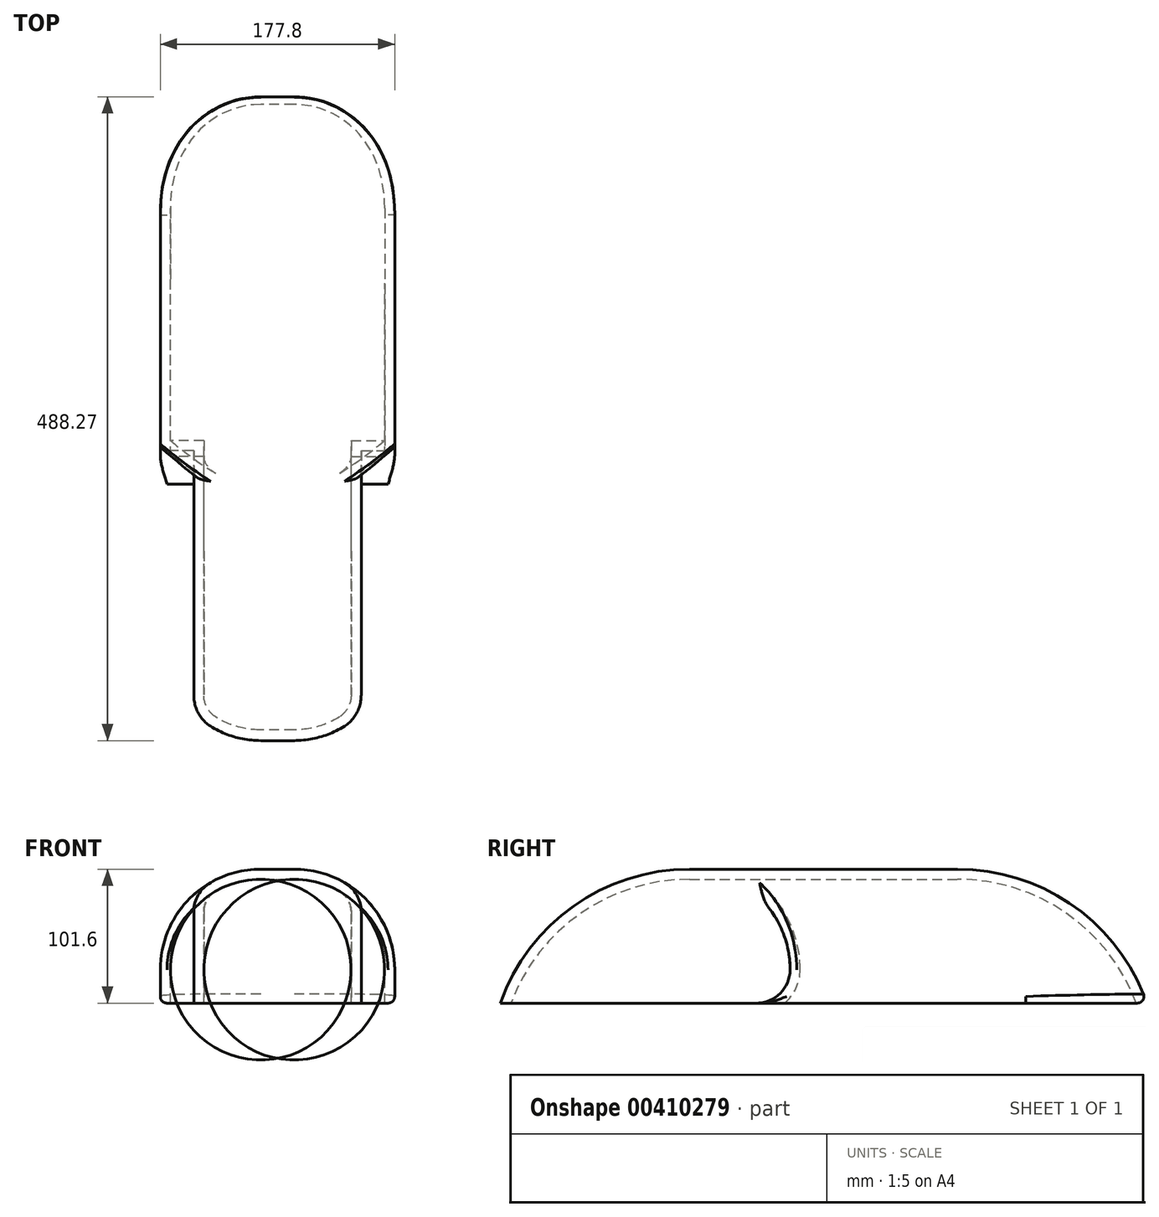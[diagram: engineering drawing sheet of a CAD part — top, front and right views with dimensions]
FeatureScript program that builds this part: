
annotation { "Feature Type Name" : "Feature", "Feature Type Description" : "" }
export const myFeature = defineFeature(function(context is Context, id is Id, definition is map)
    precondition{}
    {
        {
            var Q0;
            Q0=qCreatedBy(makeId("Right.planeOp"),FACE);
            var sketch = newSketch(context, id + "F0", { "sketchPlane" : qUnion([Q0])});
            skLineSegment(sketch, "E0.bottom", {"start": v(8.72, 0) * mm, "end": v(499.28, 0) * mm});
            skLineSegment(sketch, "E0.top", {"start": v(152.4, 101.6) * mm, "end": v(355.6, 101.6) * mm});
            skPoint(sketch, "E1.visualSharp", {"position": v(0, 101.6) * mm});
            skArc(sketch, "E1.filletArc", {"start": v(152.4, 101.6) * mm, "mid": v(64.41, 73.63) * mm, "end": v(8.72, 0) * mm});
            skPoint(sketch, "E2.visualSharp", {"position": v(508, 101.6) * mm});
            skArc(sketch, "E2.filletArc", {"start": v(499.28, 0) * mm, "mid": v(443.59, 73.63) * mm, "end": v(355.6, 101.6) * mm});
            skPoint(sketch, "E3.orphan", {"position": v(0, 0) * mm});
            skSolve(sketch);
        }
        {
            var Q0;
            Q0=makeQuery(id+"F0.imprint","IMPRINT",FACE,{"disambiguationData":[TD([[makeQuery(id+"F0.imprint","IMPRINT",EDGE,{"derivedFrom":sQuery(id+"F0.wireOp",EDGE,"E0.bottom")}),1.0]])]});
            extrude(context, id + "F1", {"entities" : qUnion([Q0]), "depth" : 177.8 * mm});
        }
        {
            var Q0;
            Q0=makeQuery(id+"F1.opExtrude","CAP_EDGE",EDGE,{"disambiguationData":[OSD([sQuery(id+"F0.wireOp",EDGE,"E1.filletArc")])],"isStart":false});
            var Q1;
            Q1=makeQuery(id+"F1.opExtrude","CAP_EDGE",EDGE,{"disambiguationData":[OSD([sQuery(id+"F0.wireOp",EDGE,"E0.top")])],"isStart":false});
            var Q2;
            Q2=makeQuery(id+"F1.opExtrude","CAP_EDGE",EDGE,{"disambiguationData":[OSD([sQuery(id+"F0.wireOp",EDGE,"E2.filletArc")])],"isStart":false});
            var Q3;
            Q3=makeQuery(id+"F1.opExtrude","CAP_EDGE",EDGE,{"disambiguationData":[OSD([sQuery(id+"F0.wireOp",EDGE,"E2.filletArc")])],"isStart":true});
            var Q4;
            Q4=makeQuery(id+"F1.opExtrude","CAP_EDGE",EDGE,{"disambiguationData":[OSD([sQuery(id+"F0.wireOp",EDGE,"E0.top")])],"isStart":true});
            var Q5;
            Q5=makeQuery(id+"F1.opExtrude","CAP_EDGE",EDGE,{"disambiguationData":[OSD([sQuery(id+"F0.wireOp",EDGE,"E1.filletArc")])],"isStart":true});
            fillet(context, id + "F2", {"entities" : qUnion([Q0, Q1, Q2, Q3, Q4, Q5]), "radius" : 76.2 * mm, "tangentPropagation" : true, "allowEdgeOverflow" : false});
        }
        {
            var Q0;
            Q0=qCreatedBy(makeId("Right.planeOp"),FACE);
            cPlane(context, id + "F3", {"entities" : qUnion([Q0]), "cplaneType" : CPlaneType.OFFSET, "offset" : 101.6 * mm, "width" : 152.4 * mm, "height" : 152.4 * mm});
        }
        {
            var Q0;
            Q0=qCreatedBy(id+"F3.planeOp",FACE);
            cPlane(context, id + "F4", {"entities" : qUnion([Q0]), "cplaneType" : CPlaneType.OFFSET, "offset" : 101.6 * mm, "width" : 152.4 * mm, "height" : 152.4 * mm});
        }
        {
            var Q0;
            Q0=qCreatedBy(id+"F4.planeOp",FACE);
            var sketch = newSketch(context, id + "F5", { "sketchPlane" : qUnion([Q0])});
            skLineSegment(sketch, "E4.bottom", {"start": v(8.71, 0) * mm, "end": v(203.2, 0) * mm});
            skLineSegment(sketch, "E4.top", {"start": v(152.4, 101.6) * mm, "end": v(152.4, 101.6) * mm});
            skLineSegment(sketch, "E4.right", {"start": v(228.6, 25.4) * mm, "end": v(228.6, 25.4) * mm});
            skPoint(sketch, "E5.visualSharp", {"position": v(0, 101.6) * mm});
            skArc(sketch, "E5.filletArc", {"start": v(152.4, 101.6) * mm, "mid": v(64.4, 73.63) * mm, "end": v(8.71, 0) * mm});
            skPoint(sketch, "E6.visualSharp", {"position": v(228.6, 101.6) * mm});
            skArc(sketch, "E6.filletArc", {"start": v(228.6, 25.4) * mm, "mid": v(206.28, 79.28) * mm, "end": v(152.4, 101.6) * mm});
            skPoint(sketch, "E7.visualSharp", {"position": v(228.6, 0) * mm});
            skArc(sketch, "E7.filletArc", {"start": v(203.2, 0) * mm, "mid": v(221.16, 7.44) * mm, "end": v(228.6, 25.4) * mm});
            skPoint(sketch, "E8.orphan", {"position": v(0, 0) * mm});
            skSolve(sketch);
        }
        {
            var Q0;
            Q0 = qSketchRegion(id + "F5", true);
            extrude(context, id + "F6", {"entities" : qUnion([Q0]), "operationType" : NewBodyOperationType.REMOVE, "oppositeDirection" : true, "depth" : 50.8 * mm});
        }
        {
            var Q0;
            Q0=qCreatedBy(makeId("Right.planeOp"),FACE);
            var sketch = newSketch(context, id + "F7", { "sketchPlane" : qUnion([Q0])});
            skLineSegment(sketch, "E9.bottom", {"start": v(8.71, 0) * mm, "end": v(203.2, 0) * mm});
            skLineSegment(sketch, "E9.top", {"start": v(152.4, 101.6) * mm, "end": v(152.4, 101.6) * mm});
            skLineSegment(sketch, "E9.right", {"start": v(228.6, 25.4) * mm, "end": v(228.6, 25.4) * mm});
            skPoint(sketch, "E10.visualSharp", {"position": v(0, 101.6) * mm});
            skArc(sketch, "E10.filletArc", {"start": v(152.4, 101.6) * mm, "mid": v(64.4, 73.63) * mm, "end": v(8.71, 0) * mm});
            skPoint(sketch, "E11.visualSharp", {"position": v(228.6, 101.6) * mm});
            skArc(sketch, "E11.filletArc", {"start": v(228.6, 25.4) * mm, "mid": v(206.28, 79.28) * mm, "end": v(152.4, 101.6) * mm});
            skPoint(sketch, "E12.visualSharp", {"position": v(228.6, 0) * mm});
            skArc(sketch, "E12.filletArc", {"start": v(203.2, 0) * mm, "mid": v(221.16, 7.44) * mm, "end": v(228.6, 25.4) * mm});
            skPoint(sketch, "E13.orphan", {"position": v(0, 0) * mm});
            skSolve(sketch);
        }
        {
            var Q0;
            Q0 = qSketchRegion(id + "F7", true);
            extrude(context, id + "F8", {"entities" : qUnion([Q0]), "operationType" : NewBodyOperationType.REMOVE, "depth" : 25.4 * mm});
        }
        {
            var Q0;
            {var subQ0=sQuery(id+"F0.wireOp",EDGE,"E1.filletArc");Q0=makeQuery(id+"F6.boolean.opBoolean","INTERSECT",EDGE,{"derivedFrom":[makeQuery(id+"F2.opFillet","BLEND_FACE",FACE,{"disambiguationData":[OSD([subQ0]),TDD([makeQuery(id+"F1.opExtrude","CAP_EDGE",EDGE,{"disambiguationData":[OSD([subQ0])],"isStart":false})])]}),makeQuery(id+"F6.opExtrude","CAP_FACE",FACE,{"disambiguationData":[OSD([sQuery(id+"F5.wireOp",EDGE,"E4.bottom"),sQuery(id+"F5.wireOp",EDGE,"E4.top"),sQuery(id+"F5.wireOp",EDGE,"E5.filletArc"),sQuery(id+"F5.wireOp",EDGE,"E6.filletArc"),sQuery(id+"F5.wireOp",EDGE,"E7.filletArc")])],"isStart":false})]});}
            var Q1;
            {var subQ0=sQuery(id+"F0.wireOp",EDGE,"E0.top");Q1=makeQuery(id+"F6.boolean.opBoolean","INTERSECT",EDGE,{"derivedFrom":[makeQuery(id+"F2.opFillet","BLEND_FACE",FACE,{"disambiguationData":[OSD([subQ0]),TDD([makeQuery(id+"F1.opExtrude","CAP_EDGE",EDGE,{"disambiguationData":[OSD([subQ0])],"isStart":false})])]}),makeQuery(id+"F6.opExtrude","CAP_FACE",FACE,{"disambiguationData":[OSD([sQuery(id+"F5.wireOp",EDGE,"E4.bottom"),sQuery(id+"F5.wireOp",EDGE,"E4.top"),sQuery(id+"F5.wireOp",EDGE,"E5.filletArc"),sQuery(id+"F5.wireOp",EDGE,"E6.filletArc"),sQuery(id+"F5.wireOp",EDGE,"E7.filletArc")])],"isStart":false})]});}
            var Q2;
            {var subQ0=sQuery(id+"F0.wireOp",EDGE,"E1.filletArc");Q2=makeQuery(id+"F8.boolean.opBoolean","INTERSECT",EDGE,{"derivedFrom":[makeQuery(id+"F2.opFillet","BLEND_FACE",FACE,{"disambiguationData":[OSD([subQ0]),TDD([makeQuery(id+"F1.opExtrude","CAP_EDGE",EDGE,{"disambiguationData":[OSD([subQ0])],"isStart":true})])]}),makeQuery(id+"F8.opExtrude","CAP_FACE",FACE,{"disambiguationData":[OSD([sQuery(id+"F7.wireOp",EDGE,"E9.bottom"),sQuery(id+"F7.wireOp",EDGE,"E9.top"),sQuery(id+"F7.wireOp",EDGE,"E10.filletArc"),sQuery(id+"F7.wireOp",EDGE,"E11.filletArc"),sQuery(id+"F7.wireOp",EDGE,"E12.filletArc")])],"isStart":false})]});}
            var Q3;
            {var subQ0=sQuery(id+"F0.wireOp",EDGE,"E0.top");Q3=makeQuery(id+"F8.boolean.opBoolean","INTERSECT",EDGE,{"derivedFrom":[makeQuery(id+"F2.opFillet","BLEND_FACE",FACE,{"disambiguationData":[OSD([subQ0]),TDD([makeQuery(id+"F1.opExtrude","CAP_EDGE",EDGE,{"disambiguationData":[OSD([subQ0])],"isStart":true})])]}),makeQuery(id+"F8.opExtrude","CAP_FACE",FACE,{"disambiguationData":[OSD([sQuery(id+"F7.wireOp",EDGE,"E9.bottom"),sQuery(id+"F7.wireOp",EDGE,"E9.top"),sQuery(id+"F7.wireOp",EDGE,"E10.filletArc"),sQuery(id+"F7.wireOp",EDGE,"E11.filletArc"),sQuery(id+"F7.wireOp",EDGE,"E12.filletArc")])],"isStart":false})]});}
            fillet(context, id + "F9", {"entities" : qUnion([Q0, Q1, Q2, Q3]), "radius" : 25.4 * mm, "tangentPropagation" : true, "allowEdgeOverflow" : false});
        }
        {
            var Q0;
            {var subQ0=sQuery(id+"F0.wireOp",EDGE,"E0.top");Q0=makeQuery(id+"F6.boolean.opBoolean","INTERSECT",EDGE,{"derivedFrom":[makeQuery(id+"F2.opFillet","BLEND_FACE",FACE,{"disambiguationData":[OSD([subQ0]),TDD([makeQuery(id+"F1.opExtrude","CAP_EDGE",EDGE,{"disambiguationData":[OSD([subQ0])],"isStart":false})])]}),makeQuery(id+"F6.opExtrude","SWEPT_FACE",FACE,{"disambiguationData":[OSD([sQuery(id+"F5.wireOp",EDGE,"E6.filletArc")])]})]});}
            var Q1;
            Q1=makeQuery(id+"F6.boolean.opBoolean","COPY",EDGE,{"derivedFrom":makeQuery(id+"F6.opExtrude","CAP_EDGE",EDGE,{"disambiguationData":[OSD([sQuery(id+"F5.wireOp",EDGE,"E7.filletArc")])],"isStart":true})});
            var Q2;
            Q2=makeQuery(id+"F2.opFillet","BLEND_EDGE",EDGE,{"blendedFrom":[makeQuery(id+"F1.opExtrude","CAP_EDGE",EDGE,{"disambiguationData":[OSD([sQuery(id+"F0.wireOp",EDGE,"E2.filletArc")])],"isStart":false}),makeQuery(id+"F1.opExtrude","SWEPT_FACE",FACE,{"disambiguationData":[OSD([sQuery(id+"F0.wireOp",EDGE,"E0.bottom")])]})],"blendedInto":[makeQuery(id+"F1.opExtrude","SWEPT_FACE",FACE,{"disambiguationData":[OSD([sQuery(id+"F0.wireOp",EDGE,"E0.bottom")])]})]});
            var Q3;
            {var subQ0=sQuery(id+"F0.wireOp",EDGE,"E0.top");Q3=makeQuery(id+"F8.boolean.opBoolean","INTERSECT",EDGE,{"derivedFrom":[makeQuery(id+"F2.opFillet","BLEND_FACE",FACE,{"disambiguationData":[OSD([subQ0]),TDD([makeQuery(id+"F1.opExtrude","CAP_EDGE",EDGE,{"disambiguationData":[OSD([subQ0])],"isStart":true})])]}),makeQuery(id+"F8.opExtrude","SWEPT_FACE",FACE,{"disambiguationData":[OSD([sQuery(id+"F7.wireOp",EDGE,"E11.filletArc")])]})]});}
            var Q4;
            Q4=makeQuery(id+"F8.boolean.opBoolean","COPY",EDGE,{"derivedFrom":makeQuery(id+"F8.opExtrude","CAP_EDGE",EDGE,{"disambiguationData":[OSD([sQuery(id+"F7.wireOp",EDGE,"E12.filletArc")])],"isStart":true})});
            fillet(context, id + "F10", {"entities" : qUnion([Q0, Q1, Q2, Q3, Q4]), "radius" : 5.08 * mm, "tangentPropagation" : true, "allowEdgeOverflow" : false});
        }
        {
            var Q0;
            Q0=makeQuery(id+"F1.opExtrude","SWEPT_FACE",FACE,{"disambiguationData":[OSD([sQuery(id+"F0.wireOp",EDGE,"E0.bottom")])]});
            shell(context, id + "F11", {"entities" : qUnion([Q0]), "thickness" : 7.62 * mm});
        }
    });
